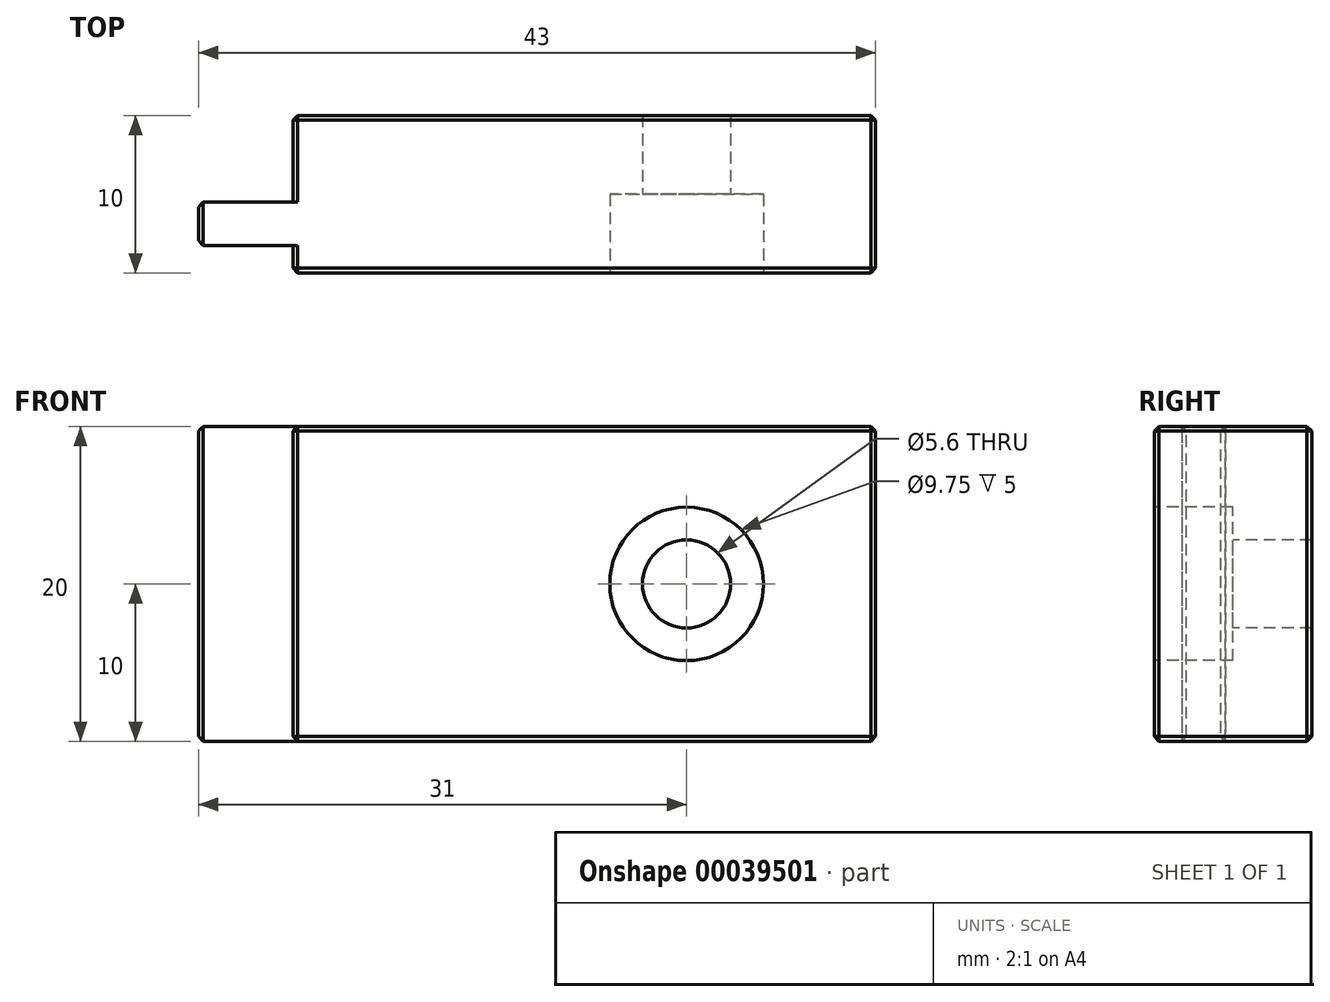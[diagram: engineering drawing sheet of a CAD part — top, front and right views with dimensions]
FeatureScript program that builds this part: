
annotation { "Feature Type Name" : "Feature", "Feature Type Description" : "" }
export const myFeature = defineFeature(function(context is Context, id is Id, definition is map)
    precondition{}
    {
        {
            var Q0;
            Q0=qCreatedBy(makeId("Front.planeOp"),FACE);
            var sketch = newSketch(context, id + "F0", { "sketchPlane" : qUnion([Q0])});
            skLineSegment(sketch, "E0.bottom", {"start": v(-18.5, 10) * mm, "end": v(18.5, 10) * mm});
            skLineSegment(sketch, "E0.top", {"start": v(-18.5, -10) * mm, "end": v(18.5, -10) * mm});
            skLineSegment(sketch, "E0.left", {"start": v(-18.5, 10) * mm, "end": v(-18.5, -10) * mm});
            skLineSegment(sketch, "E0.right", {"start": v(18.5, 10) * mm, "end": v(18.5, -10) * mm});
            skPoint(sketch, "E1.centerSnap0", {"position": v(18.5, 0) * mm});
            skPoint(sketch, "E2", {"position": v(6.5, 0) * mm});
            skSolve(sketch);
        }
        {
            var Q0;
            Q0 = qSketchRegion(id + "F0", true);
            extrude(context, id + "F1", {"entities" : qUnion([Q0]), "oppositeDirection" : true, "depth" : 10 * mm});
        }
        {
            var Q0;
            Q0=sQuery(id+"F0.wireOp",VERTEX,"E2");
            var Q1;
            Q1=makeQuery(id+"F1.opExtrude","SWEPT_BODY",BODY,{"disambiguationData":[OSD([sQuery(id+"F0.wireOp",EDGE,"E0.bottom"),sQuery(id+"F0.wireOp",EDGE,"E0.top"),sQuery(id+"F0.wireOp",EDGE,"E0.left"),sQuery(id+"F0.wireOp",EDGE,"E0.right")])]});
            hole(context, id + "F2", {"style" : HoleStyle.C_BORE, "holeDiameter" : 5.6 * mm, "cBoreDiameter" : 9.75 * mm, "cBoreDepth" : 5 * mm, "endStyle" : HoleEndStyle.THROUGH, "locations" : qUnion([Q0]), "scope" : qUnion([Q1])});
        }
        {
            var Q0;
            Q0=makeQuery(id+"F1.opExtrude","SWEPT_FACE",FACE,{"disambiguationData":[OSD([sQuery(id+"F0.wireOp",EDGE,"E0.left")])]});
            var sketch = newSketch(context, id + "F3", { "sketchPlane" : qUnion([Q0])});
            skLineSegment(sketch, "E3.bottom", {"start": v(-4.5, 10) * mm, "end": v(-1.75, 10) * mm});
            skLineSegment(sketch, "E3.top", {"start": v(-4.5, -10) * mm, "end": v(-1.75, -10) * mm});
            skLineSegment(sketch, "E3.left", {"start": v(-4.5, 10) * mm, "end": v(-4.5, -10) * mm});
            skLineSegment(sketch, "E3.right", {"start": v(-1.75, 10) * mm, "end": v(-1.75, -10) * mm});
            skSolve(sketch);
        }
        {
            var Q0;
            Q0 = qSketchRegion(id + "F3", true);
            extrude(context, id + "F4", {"entities" : qUnion([Q0]), "operationType" : NewBodyOperationType.ADD, "depth" : 6 * mm});
        }
        {
            var Q0;
            Q0=makeQuery(id+"F2.hole-0.boolean.opBoolean","COPY",EDGE,{"derivedFrom":makeQuery(id+"F2.hole-0.opRevolve","SWEPT_EDGE",EDGE,{"disambiguationData":[OSD([sQuery(id+"F2.hole-0.sketch.wireOp",EDGE,"cbore_start_line_2"),sQuery(id+"F2.hole-0.sketch.wireOp",EDGE,"cbore_start_line_3")])]})});
            var Q1;
            Q1=makeQuery(id+"F1.opExtrude","CAP_EDGE",EDGE,{"disambiguationData":[OSD([sQuery(id+"F0.wireOp",EDGE,"E0.bottom")])],"isStart":true});
            var Q2;
            Q2=makeQuery(id+"F1.opExtrude","CAP_EDGE",EDGE,{"disambiguationData":[OSD([sQuery(id+"F0.wireOp",EDGE,"E0.left")])],"isStart":true});
            var Q3;
            Q3=makeQuery(id+"F1.opExtrude","CAP_EDGE",EDGE,{"disambiguationData":[OSD([sQuery(id+"F0.wireOp",EDGE,"E0.top")])],"isStart":true});
            var Q4;
            Q4=makeQuery(id+"F1.opExtrude","CAP_EDGE",EDGE,{"disambiguationData":[OSD([sQuery(id+"F0.wireOp",EDGE,"E0.right")])],"isStart":true});
            var Q5;
            Q5=makeQuery(id+"F1.opExtrude","SWEPT_EDGE",EDGE,{"disambiguationData":[OSD([sQuery(id+"F0.wireOp",EDGE,"E0.top"),sQuery(id+"F0.wireOp",EDGE,"E0.right")])]});
            var Q6;
            Q6=makeQuery(id+"F1.opExtrude","SWEPT_EDGE",EDGE,{"disambiguationData":[OSD([sQuery(id+"F0.wireOp",EDGE,"E0.bottom"),sQuery(id+"F0.wireOp",EDGE,"E0.right")])]});
            var Q7;
            {var subQ0=sQuery(id+"F0.wireOp",EDGE,"E0.top");var subQ1=sQuery(id+"F0.wireOp",EDGE,"E0.left");Q7=makeQuery(id+"F4.boolean.opBoolean","SPLIT",EDGE,{"disambiguationData":[TD([makeQuery(id+"F4.opExtrude","SWEPT_FACE",FACE,{"disambiguationData":[OSD([sQuery(id+"F3.wireOp",EDGE,"E3.right")])]})])],"derivedFrom":makeQuery(id+"F1.opExtrude","SWEPT_EDGE",EDGE,{"disambiguationData":[OSD([subQ0,subQ1])]})});}
            var Q8;
            {var subQ0=sQuery(id+"F0.wireOp",EDGE,"E0.top");var subQ1=sQuery(id+"F0.wireOp",EDGE,"E0.left");Q8=makeQuery(id+"F4.boolean.opBoolean","SPLIT",EDGE,{"disambiguationData":[TD([makeQuery(id+"F4.opExtrude","SWEPT_FACE",FACE,{"disambiguationData":[OSD([sQuery(id+"F3.wireOp",EDGE,"E3.left")])]})])],"derivedFrom":makeQuery(id+"F1.opExtrude","SWEPT_EDGE",EDGE,{"disambiguationData":[OSD([subQ0,subQ1])]})});}
            var Q9;
            Q9=makeQuery(id+"F4.opExtrude","CAP_EDGE",EDGE,{"disambiguationData":[OSD([sQuery(id+"F3.wireOp",EDGE,"E3.top")])],"isStart":false});
            var Q10;
            Q10=makeQuery(id+"F4.opExtrude","CAP_EDGE",EDGE,{"disambiguationData":[OSD([sQuery(id+"F3.wireOp",EDGE,"E3.bottom")])],"isStart":false});
            var Q11;
            {var subQ0=sQuery(id+"F0.wireOp",EDGE,"E0.bottom");var subQ1=sQuery(id+"F0.wireOp",EDGE,"E0.left");Q11=makeQuery(id+"F4.boolean.opBoolean","SPLIT",EDGE,{"disambiguationData":[TD([makeQuery(id+"F4.opExtrude","SWEPT_FACE",FACE,{"disambiguationData":[OSD([sQuery(id+"F3.wireOp",EDGE,"E3.right")])]})])],"derivedFrom":makeQuery(id+"F1.opExtrude","SWEPT_EDGE",EDGE,{"disambiguationData":[OSD([subQ0,subQ1])]})});}
            var Q12;
            {var subQ0=sQuery(id+"F0.wireOp",EDGE,"E0.bottom");var subQ1=sQuery(id+"F0.wireOp",EDGE,"E0.left");Q12=makeQuery(id+"F4.boolean.opBoolean","SPLIT",EDGE,{"disambiguationData":[TD([makeQuery(id+"F4.opExtrude","SWEPT_FACE",FACE,{"disambiguationData":[OSD([sQuery(id+"F3.wireOp",EDGE,"E3.left")])]})])],"derivedFrom":makeQuery(id+"F1.opExtrude","SWEPT_EDGE",EDGE,{"disambiguationData":[OSD([subQ0,subQ1])]})});}
            var Q13;
            Q13=makeQuery(id+"F4.opExtrude","CAP_EDGE",EDGE,{"disambiguationData":[OSD([sQuery(id+"F3.wireOp",EDGE,"E3.right")])],"isStart":false});
            var Q14;
            Q14=makeQuery(id+"F4.opExtrude","CAP_EDGE",EDGE,{"disambiguationData":[OSD([sQuery(id+"F3.wireOp",EDGE,"E3.left")])],"isStart":false});
            var Q15;
            Q15=makeQuery(id+"F1.opExtrude","CAP_EDGE",EDGE,{"disambiguationData":[OSD([sQuery(id+"F0.wireOp",EDGE,"E0.left")])],"isStart":false});
            var Q16;
            Q16=makeQuery(id+"F1.opExtrude","CAP_EDGE",EDGE,{"disambiguationData":[OSD([sQuery(id+"F0.wireOp",EDGE,"E0.bottom")])],"isStart":false});
            var Q17;
            Q17=makeQuery(id+"F1.opExtrude","CAP_EDGE",EDGE,{"disambiguationData":[OSD([sQuery(id+"F0.wireOp",EDGE,"E0.top")])],"isStart":false});
            var Q18;
            Q18=makeQuery(id+"F1.opExtrude","CAP_EDGE",EDGE,{"disambiguationData":[OSD([sQuery(id+"F0.wireOp",EDGE,"E0.right")])],"isStart":false});
            chamfer(context, id + "F5", {"entities" : qUnion([Q0, Q1, Q2, Q3, Q4, Q5, Q6, Q7, Q8, Q9, Q10, Q11, Q12, Q13, Q14, Q15, Q16, Q17, Q18]), "width" : .3 * mm, "tangentPropagation" : true});
        }
    });
